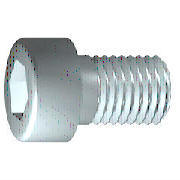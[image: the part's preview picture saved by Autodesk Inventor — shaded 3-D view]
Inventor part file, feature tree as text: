
AUTODESK INVENTOR PART (.ipt)
format: ipt  version: 2022 (Build 260153000, 153)  size: 187,904 bytes
history: native  units: mm (DEFAULTED — no unit token found)
features: sketch x2, other x1, extrude x1, plane x1, fillet x1
ambient origin geometry x7: Origin, YZ Plane, XY Plane, X Axis, Y Axis, Z Axis, Center Point
bodies: Solid1 (feature_tree)
feature tree (6):
  other  "Körper"
  extrude  "Loch"  Depth=3.0mm
  plane  "Work Plane1"
  fillet  "Fillet2"  Radius=3.0mm
  sketch  "Skizze1"  dims[d1=18.0mm d2=0.306825mm d3=3.0mm]
  sketch  "Skizze2"  dims[d4=1.3mm d5=60.0deg d6=3.0mm d7=3.0mm d8=2.886751mm d9=5.5mm d10=90.0deg d11=10.0mm d12=0.0mm d13=18.0mm d14=0.0mm d15=0.306725mm d16=0.306725mm d17=0.3mm d19=0.0mm d26=30.0mm d27=45.0deg d28=0.0mm d29=0.0mm d30=0.1mm]
